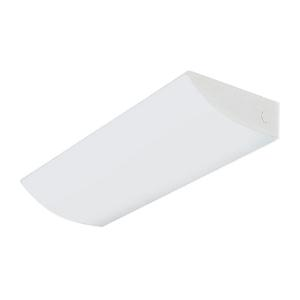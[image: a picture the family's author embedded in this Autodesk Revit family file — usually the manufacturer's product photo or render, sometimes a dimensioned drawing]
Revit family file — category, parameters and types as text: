
# Revit family: 3f_filippi_-_mira_par_ind_3f_filippi_-_1960_-_mira_par_led_4x12w_dali_ind_l675
name_source: partatom
category: Lighting Fixtures
units: mm (PartAtom-declared; Revit-internal decimal feet)

## family parameters
Cut with Voids When Loaded = No
Host = Face
Light Source = No
Part Type = Normal
Room Calculation Point = No
Round Connector Dimension = Use Diameter
Shared = No

## types (1)
- 3F Filippi - Mira Par Ind (1 x LED, 6840 lm, 54 W, 4000 K)
    Apparent Load = 54 VA
    Approval mark = ENEC
    CIE Flux Codes = - - - 0 100
    Color Rendering = 80
    Color Temperature = 4000 K
    Control Gear = Electronic transformer
    Default Elevation = 1800 mm
    Description = ILLUMINOTECHNICAL
Luminous efficiency 100% (DLOR 0%, ULOR 100%).
Initial luminous flux of the luminaire 6840 lm.
Asymmetric indirect distribution.
Beam angle: 77° - 106°.
Luminous efficacy 127 lm/W.
Lifetime (L93/B10): 30000 h. (tq+25°C)
Lifetime (L90/B10): 50000 h. (tq+25°C)
Lifetime (L85/B10): 80000 h. (tq+25°C)
Lifetime (L80/B10): 100000 h. (tq+25°C)
Sudden decreased luminous flux after 50000 hours: 0% (C0).
Photobiological safety in compliance with IEC/TR 62778: RG0 risk exempt, (IEC 62471).
In compliance with IEC/EN 62722-2-1 - IEC/EN 62717 standards.

SOURCE
4 linear LED modules 12W/840.
Energy efficiency class (UE 2019/2020 - UE 2019/2015): D.
CIE 13.3 Colour rendering index: CRI >80 (R9 <50%).
IES TM-30 Fidelity Index: Rf = 84 Rg = 95.
CCT nominal colour temperature 4000 K.
Colour initial tolerance (MacAdam): SDCM 3.

MECHANICAL
Housing in white painted steel.
Asymmetric flow recuperator, high efficiency, in specular aluminium with superficial titanium-magnesium treatment.
Upper diffuser in transparent polycarbonate, self-extinguishing V2, UV stabilised.
Luminaire with limited surface temperature. - D - (EN 60598-2-24)
Dimensions: 675x230 mm, height 80 mm. Weight 2.58 kg.
IP40 protection degree.
Glow-wire test resistance 850°C.

ELECTRICAL
Halogen Free DALI-2, PUSH-DIM, electronic wiring 230V-50/60Hz, power factor 0.95 at full load, THD <25%, constant output current, SELV, class I, 1 driver, 1 DALI addresse.
Power of the luminaire 54 W.
CE - IEC 60598-1 - EN 60598-1.
SAFE FLICKER: PstLM=<1 and SVM=<0.4 (IEC TR 61547-1 and IEC TR 63158), to ensure a more comfortable and safe light.
Luminaire compliant with EN 60598-2-22 for power supply from a centralised emergency system CPSS (Central Power Supply System), not incorporated in the luminaire - high risk areas excluded. The default power and flux are 100% in AC and 15% in DC.
Ambient temperature from 0°C to +25°C.
Temperature class T6 max 85°C.
Relative humidity UR: <85%.

INSTALLATION
Wall.
All accessories dedicated to this product are available on the Catalog and on our website www.3F-Filippi.com.

APPLICATIONS
Environments where a comfortable light is required. Luminaire for wall mounting, with an essential and modern design. Suitable for offices, conference rooms, managerial offices.

LIGHT MANAGEMENT
Recommended minimum setting: 10%.
The device, equipped with DALI-2 driver, can be controlled manually with 3F Easy Dim technology or automatically/manually with 3F Smart Dimming technology and/or centralised DALI systems.
DALI-2 certification guarantees interoperability with other devices with the same certification.
In electrical systems without a regulation system (manual or automatic) and DALI bus, a suitable jumper must be made on the DA-DA terminals of the appliance.

WARNING
Luminaire designed for disposal/recycling at end-of-life.
Replaceable (LED only) light source by a professional. Replaceable control gear by a professional.
    Height = 80 mm  [stored 0.262467 ft]
    Lamp = 1 x LED
    Lamp Light Flux = 6840 lm
    Lamp Power = 54 W
    Lamp count = 1
    Length = 675 mm
    Lifetime = 50000 h
    Luminous efficacy = 127 lm/W
    Manufacturer = 3F Filippi
    ModVariant = No
    Model = 3F Filippi - 1960 - Mira Par LED 4x12W DALI IND L675
    Mounting Place = Wall
    Mounting Type = Surface mounted
    Number of Poles = 1
    OnlyDefault = Yes
    Power Factor = 1
    Product Name = 3F Filippi - Mira Par Ind
    Product group = wall-mounted luminaire
    ProductGroupID = 20
    Protection Class = Protection class I
    Protection Degree = IP 40
    RLX_Detail_Level = 1
    RLX_Emergency_Light_Flux = 0 lm
    RLX_Emergency_Type = 0
    RLX_Emergency_Type_DB = No
    RlxData = <blob elided: 33821 chars, md5=4f6fbeed>
    Socket = socket
    Standby Power = 0 W
    System Light Flux = 6840 lm
    System Power = 54 W
    Type Comments = Product without accessories
    Type Image = 3ffilippi_mira_par_ind.jpg
    URL = http://relux.com
    VarID = ---
    Voltage = 0 V
    Weight = 0.00 kg
    Width = 230 mm

note: [stored X ft] marks values corroborated as IEEE doubles in the binary element streams (Revit-internal decimal feet)

## geometry (parser evidence)
native form markers: Blend x4, Sweep x10
no freeform markers — native parametric forms only
